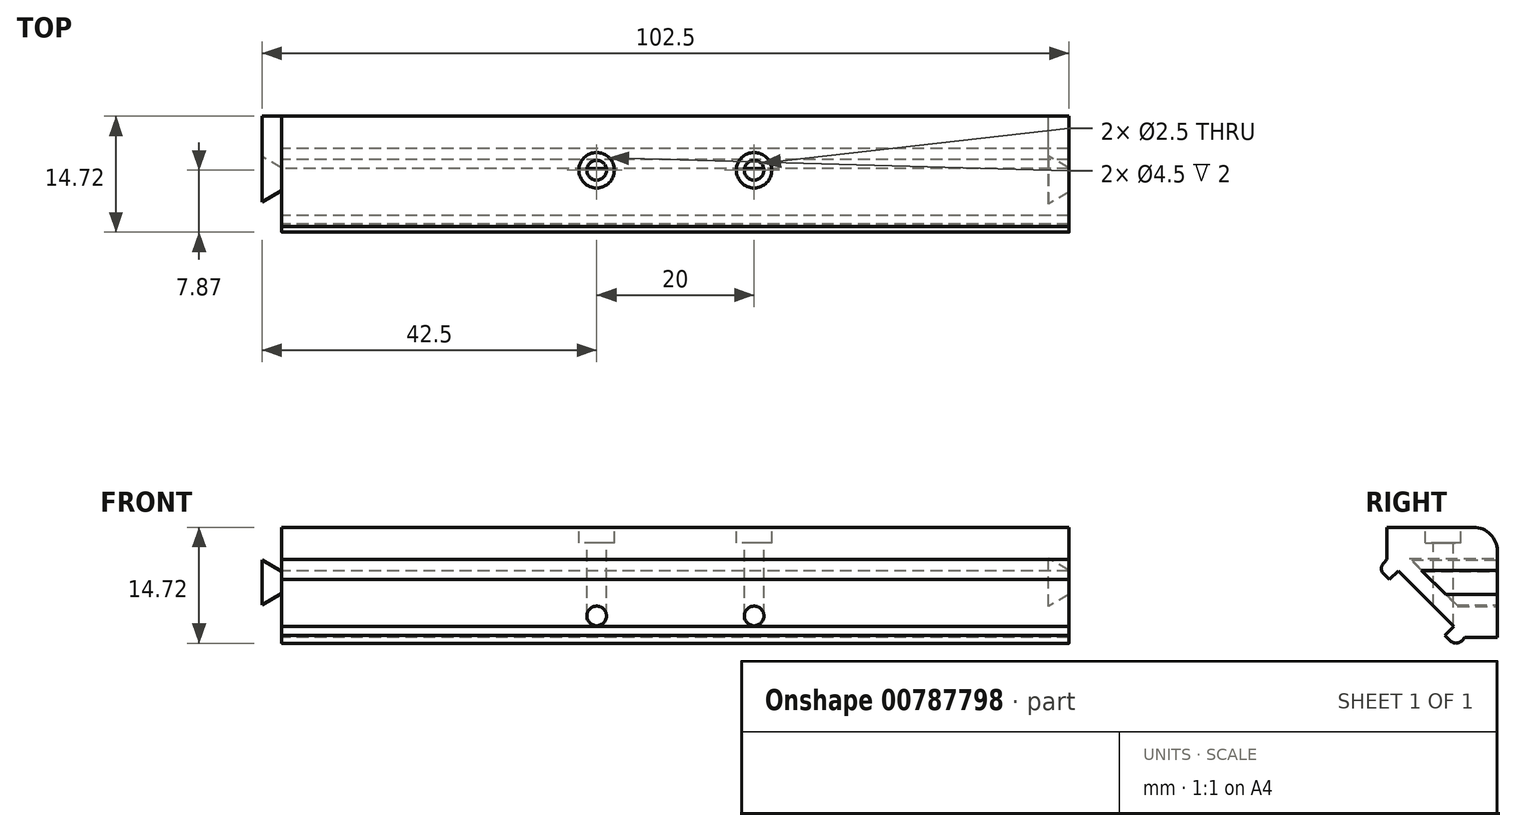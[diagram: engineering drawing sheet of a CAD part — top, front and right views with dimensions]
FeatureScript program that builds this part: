
annotation { "Feature Type Name" : "Feature", "Feature Type Description" : "" }
export const myFeature = defineFeature(function(context is Context, id is Id, definition is map)
    precondition{}
    {
        {
            var Q0;
            Q0=qCreatedBy(makeId("Right.planeOp"),FACE);
            var sketch = newSketch(context, id + "F0", { "sketchPlane" : qUnion([Q0])});
            skLineSegment(sketch, "E0", {"start": v(-4.1, -14) * mm, "end": v(-14, -4.1) * mm});
            skPoint(sketch, "E1.visualSharp", {"position": v(0, 0) * mm});
            skArc(sketch, "E1.filletArc", {"start": v(0, -3) * mm, "mid": v(-0.88, -0.88) * mm, "end": v(-3, 0) * mm});
            skLineSegment(sketch, "E2", {"start": v(-4.1, -14) * mm, "end": v(-4.52, -14.42) * mm});
            skLineSegment(sketch, "E3", {"start": v(-5.94, -14.42) * mm, "end": v(-6.65, -13.72) * mm});
            skLineSegment(sketch, "E4", {"start": v(-6.65, -13.72) * mm, "end": v(-5.51, -12.59) * mm});
            skLineSegment(sketch, "E5", {"start": v(-9.05, -9.05) * mm, "end": v(0, 0) * mm, "construction": true});
            skPoint(sketch, "E6.visualSharp", {"position": v(-5.23, -15.13) * mm});
            skArc(sketch, "E6.filletArc", {"start": v(-5.94, -14.42) * mm, "mid": v(-5.23, -14.72) * mm, "end": v(-4.52, -14.42) * mm});
            skLineSegment(sketch, "E7", {"start": v(-3, 0) * mm, "end": v(-14, 0) * mm});
            skLineSegment(sketch, "E8", {"start": v(-14, 0) * mm, "end": v(-14, -4.1) * mm});
            skLineSegment(sketch, "E9", {"start": v(0, -3) * mm, "end": v(0, -14) * mm});
            skPoint(sketch, "E9.endSnap0", {"position": v(-4.31, -14.21) * mm});
            skLineSegment(sketch, "E10", {"start": v(0, -14) * mm, "end": v(-4.1, -14) * mm});
            skLineSegment(sketch, "E11.MirrorCS", {"start": v(-14, -4.1) * mm, "end": v(-14.42, -4.52) * mm});
            skArc(sketch, "E12.MirrorCS", {"start": v(-14.42, -5.94) * mm, "mid": v(-14.72, -5.23) * mm, "end": v(-14.42, -4.52) * mm});
            skLineSegment(sketch, "E13.MirrorCS", {"start": v(-14.42, -5.94) * mm, "end": v(-13.72, -6.65) * mm});
            skLineSegment(sketch, "E14.MirrorCS", {"start": v(-13.72, -6.65) * mm, "end": v(-12.59, -5.51) * mm});
            skSolve(sketch);
        }
        {
            var Q0;
            Q0 = qSketchRegion(id + "F0", true);
            extrude(context, id + "F1", {"entities" : qUnion([Q0]), "depth" : 100 * mm, "offsetDistance" : 25 * mm});
        }
        {
            var Q0;
            Q0=makeQuery(id+"F1.opExtrude","CAP_FACE",FACE,{"disambiguationData":[OSD([sQuery(id+"F0.wireOp",EDGE,"aDCuehPR-K7hz-AYi5-jupJ-TwmlBC8FOzOA"),sQuery(id+"F0.wireOp",EDGE,"E0"),sQuery(id+"F0.wireOp",EDGE,"dTebbWda-ldcJ-0is6-tMz7-TifbNRYKdX4Z"),sQuery(id+"F0.wireOp",EDGE,"E1.filletArc"),sQuery(id+"F0.wireOp",EDGE,"E2"),sQuery(id+"F0.wireOp",EDGE,"E3"),sQuery(id+"F0.wireOp",EDGE,"E4"),sQuery(id+"F0.wireOp",EDGE,"E6.filletArc"),sQuery(id+"F0.wireOp",EDGE,"e01ae123-55d3-445e-b42b-3b43afa4eca10.MirrorCS"),sQuery(id+"F0.wireOp",EDGE,"e01ae123-55d3-445e-b42b-3b43afa4eca11.MirrorCS"),sQuery(id+"F0.wireOp",EDGE,"e01ae123-55d3-445e-b42b-3b43afa4eca12.MirrorCS"),sQuery(id+"F0.wireOp",EDGE,"e01ae123-55d3-445e-b42b-3b43afa4eca13.MirrorCS")])],"isStart":true});
            var sketch = newSketch(context, id + "F2", { "sketchPlane" : qUnion([Q0])});
            skArc(sketch, "E15.0", {"start": v(0, -3) * mm, "mid": v(0.88, -0.88) * mm, "end": v(3, 0) * mm});
            skLineSegment(sketch, "E16", {"start": v(0, -3) * mm, "end": v(0, 0) * mm});
            skLineSegment(sketch, "E17", {"start": v(0, 0) * mm, "end": v(3, 0) * mm});
            skSolve(sketch);
        }
        {
            var Q0;
            Q0=makeQuery(id+"F1.opExtrude","SWEPT_FACE",FACE,{"disambiguationData":[OSD([sQuery(id+"F0.wireOp",EDGE,"E9")])]});
            var sketch = newSketch(context, id + "F3", { "sketchPlane" : qUnion([Q0])});
            skPoint(sketch, "E18.0", {"position": v(-100, -3) * mm});
            skPoint(sketch, "E18.1", {"position": v(-100, -14) * mm});
            skLineSegment(sketch, "E19", {"start": v(-100, -3) * mm, "end": v(-100, -14) * mm, "construction": true});
            skLineSegment(sketch, "E20", {"start": v(-100, -7) * mm, "end": v(-16.73, -7) * mm, "construction": true});
            skLineSegment(sketch, "E21", {"start": v(-100, -7) * mm, "end": v(-100, -5.46) * mm});
            skLineSegment(sketch, "E22", {"start": v(-100, -5.46) * mm, "end": v(-97.4, -3.96) * mm});
            skLineSegment(sketch, "E23", {"start": v(-97.4, -3.96) * mm, "end": v(-97.4, -7) * mm});
            skLineSegment(sketch, "E24.MirrorCS", {"start": v(-100, -7) * mm, "end": v(-100, -8.54) * mm});
            skLineSegment(sketch, "E25.MirrorCS", {"start": v(-97.4, -10.04) * mm, "end": v(-97.4, -7) * mm});
            skLineSegment(sketch, "E26.MirrorCS", {"start": v(-100, -8.54) * mm, "end": v(-97.4, -10.04) * mm});
            skLineSegment(sketch, "E27", {"start": v(-50, -3) * mm, "end": v(-50, -9.9) * mm});
            skLineSegment(sketch, "E28.MirrorCS", {"start": v(0, -7) * mm, "end": v(0, -5.46) * mm, "construction": true});
            skLineSegment(sketch, "E29.MirrorCS", {"start": v(0, -7) * mm, "end": v(0, -8.54) * mm, "construction": true});
            skLineSegment(sketch, "E30.MirrorCS", {"start": v(0, -8.54) * mm, "end": v(-2.6, -10.04) * mm, "construction": true});
            skLineSegment(sketch, "E31.MirrorCS", {"start": v(-2.6, -10.04) * mm, "end": v(-2.6, -7) * mm, "construction": true});
            skLineSegment(sketch, "E32.MirrorCS", {"start": v(0, -5.46) * mm, "end": v(-2.6, -3.96) * mm, "construction": true});
            skLineSegment(sketch, "E33.MirrorCS", {"start": v(-2.6, -3.96) * mm, "end": v(-2.6, -7) * mm, "construction": true});
            skLineSegment(sketch, "E34.MirrorCS", {"start": v(0, -5.46) * mm, "end": v(2.6, -3.96) * mm, "construction": true});
            skLineSegment(sketch, "E35.MirrorCS", {"start": v(2.6, -10.04) * mm, "end": v(2.6, -7) * mm, "construction": true});
            skLineSegment(sketch, "E36.MirrorCS", {"start": v(0, -8.54) * mm, "end": v(2.6, -10.04) * mm, "construction": true});
            skLineSegment(sketch, "E37.MirrorCS", {"start": v(2.6, -3.96) * mm, "end": v(2.6, -7) * mm, "construction": true});
            skLineSegment(sketch, "E38", {"start": v(-100, -3) * mm, "end": v(0, -3) * mm, "construction": true});
            skSolve(sketch);
        }
        {
            var Q0;
            Q0 = qSketchRegion(id + "F3", true);
            var Q1;
            Q1=makeQuery(id+"F1.opExtrude","SWEPT_FACE",FACE,{"disambiguationData":[OSD([sQuery(id+"F0.wireOp",EDGE,"E0")])]});
            extrude(context, id + "F4", {"entities" : qUnion([Q0]), "operationType" : NewBodyOperationType.REMOVE, "endBound" : BoundingType.UP_TO_SURFACE, "oppositeDirection" : true, "depth" : 25 * mm, "endBoundEntityFace" : qUnion([Q1]), "hasOffset" : true, "offsetDistance" : 3 * mm});
        }
        {
            var Q0;
            Q0=makeQuery(id+"F1.opExtrude","SWEPT_FACE",FACE,{"disambiguationData":[OSD([sQuery(id+"F0.wireOp",EDGE,"E9")])]});
            var sketch = newSketch(context, id + "F5", { "sketchPlane" : qUnion([Q0])});
            skLineSegment(sketch, "E39.0", {"start": v(0, -8.42) * mm, "end": v(2.5, -9.87) * mm});
            skLineSegment(sketch, "E39.1", {"start": v(2.5, -9.87) * mm, "end": v(2.5, -4) * mm});
            skLineSegment(sketch, "E39.2", {"start": v(2.5, -4) * mm, "end": v(2.5, -4.13) * mm});
            skLineSegment(sketch, "E39.3", {"start": v(1.37, -4.79) * mm, "end": v(2.5, -4.13) * mm});
            skLineSegment(sketch, "E40.0", {"start": v(0, -7) * mm, "end": v(0, -5.46) * mm, "construction": true});
            skLineSegment(sketch, "E41", {"start": v(1.37, -4.79) * mm, "end": v(0, -5.58) * mm});
            skLineSegment(sketch, "E42.0", {"start": v(0, -7) * mm, "end": v(0, -8.54) * mm, "construction": true});
            skLineSegment(sketch, "E43", {"start": v(0, -8.42) * mm, "end": v(0, -5.58) * mm});
            skSolve(sketch);
        }
        {
            var Q0;
            Q0 = qSketchRegion(id + "F5", true);
            var Q1;
            {var subQ5=sQuery(id+"F0.wireOp",EDGE,"E4");var subQ10=sQuery(id+"F0.wireOp",EDGE,"E0");Q1=makeQuery(id+"F4.boolean.opBoolean","SPLIT",FACE,{"disambiguationData":[TD([makeQuery(id+"F1.opExtrude","SWEPT_FACE",FACE,{"disambiguationData":[OSD([subQ5])]})])],"derivedFrom":makeQuery(id+"F1.opExtrude","SWEPT_FACE",FACE,{"disambiguationData":[OSD([subQ10])]})});}
            extrude(context, id + "F6", {"entities" : qUnion([Q0]), "operationType" : NewBodyOperationType.ADD, "endBound" : BoundingType.UP_TO_SURFACE, "oppositeDirection" : true, "depth" : 25 * mm, "endBoundEntityFace" : qUnion([Q1]), "hasOffset" : true, "offsetDistance" : 3.1 * mm});
        }
        {
            var Q0;
            Q0 = qSketchRegion(id + "F2", true);
            var Q1;
            Q1=makeQuery(id+"F6.opExtrude","SWEPT_FACE",FACE,{"disambiguationData":[OSD([sQuery(id+"F5.wireOp",EDGE,"E39.1"),sQuery(id+"F5.wireOp",EDGE,"E39.2")])]});
            extrude(context, id + "F7", {"entities" : qUnion([Q0]), "operationType" : NewBodyOperationType.REMOVE, "endBound" : BoundingType.UP_TO_SURFACE, "depth" : 25 * mm, "endBoundEntityFace" : qUnion([Q1]), "offsetDistance" : 25 * mm});
        }
        {
            var Q0;
            Q0=makeQuery(id+"F1.opExtrude","SWEPT_FACE",FACE,{"disambiguationData":[OSD([sQuery(id+"F0.wireOp",EDGE,"E7")])]});
            var sketch = newSketch(context, id + "F8", { "sketchPlane" : qUnion([Q0])});
            skLineSegment(sketch, "E44.0", {"start": v(0, -14) * mm, "end": v(0, 0) * mm, "construction": true});
            skLineSegment(sketch, "E45.0", {"start": v(100, 0) * mm, "end": v(0, 0) * mm, "construction": true});
            skLineSegment(sketch, "E46", {"start": v(0, -6.85) * mm, "end": v(40, -6.85) * mm, "construction": true});
            skCircle(sketch, "E47", {"center": v(40, -6.85) * mm, "radius": 1.25 * mm});
            skPoint(sketch, "E48.0", {"position": v(100, 0) * mm});
            skLineSegment(sketch, "E49", {"start": v(50, 0) * mm, "end": v(50, -11.86) * mm, "construction": true});
            skCircle(sketch, "E50.MirrorC", {"center": v(60, -6.85) * mm, "radius": 1.25 * mm});
            skSolve(sketch);
        }
        {
            var Q0;
            Q0 = qSketchRegion(id + "F8", true);
            var Q1;
            Q1=makeQuery(id+"F1.opExtrude","SWEPT_FACE",FACE,{"disambiguationData":[OSD([sQuery(id+"F0.wireOp",EDGE,"E0")])]});
            extrude(context, id + "F9", {"entities" : qUnion([Q0]), "operationType" : NewBodyOperationType.REMOVE, "endBound" : BoundingType.UP_TO_SURFACE, "oppositeDirection" : true, "depth" : 25 * mm, "endBoundEntityFace" : qUnion([Q1]), "offsetDistance" : 25 * mm});
        }
        {
            var Q0;
            Q0=makeQuery(id+"F1.opExtrude","SWEPT_FACE",FACE,{"disambiguationData":[OSD([sQuery(id+"F0.wireOp",EDGE,"E7")])]});
            var sketch = newSketch(context, id + "F10", { "sketchPlane" : qUnion([Q0])});
            skCircle(sketch, "E51.0", {"center": v(40, -6.85) * mm, "radius": 1.25 * mm, "construction": true});
            skCircle(sketch, "E52", {"center": v(40, -6.85) * mm, "radius": 2.25 * mm});
            skCircle(sketch, "E53.0", {"center": v(60, -6.85) * mm, "radius": 1.25 * mm, "construction": true});
            skCircle(sketch, "E54", {"center": v(60, -6.85) * mm, "radius": 2.25 * mm});
            skSolve(sketch);
        }
        {
            var Q0;
            Q0 = qSketchRegion(id + "F10", true);
            extrude(context, id + "F11", {"entities" : qUnion([Q0]), "operationType" : NewBodyOperationType.REMOVE, "oppositeDirection" : true, "depth" : 2 * mm, "offsetDistance" : 25 * mm});
        }
    });
